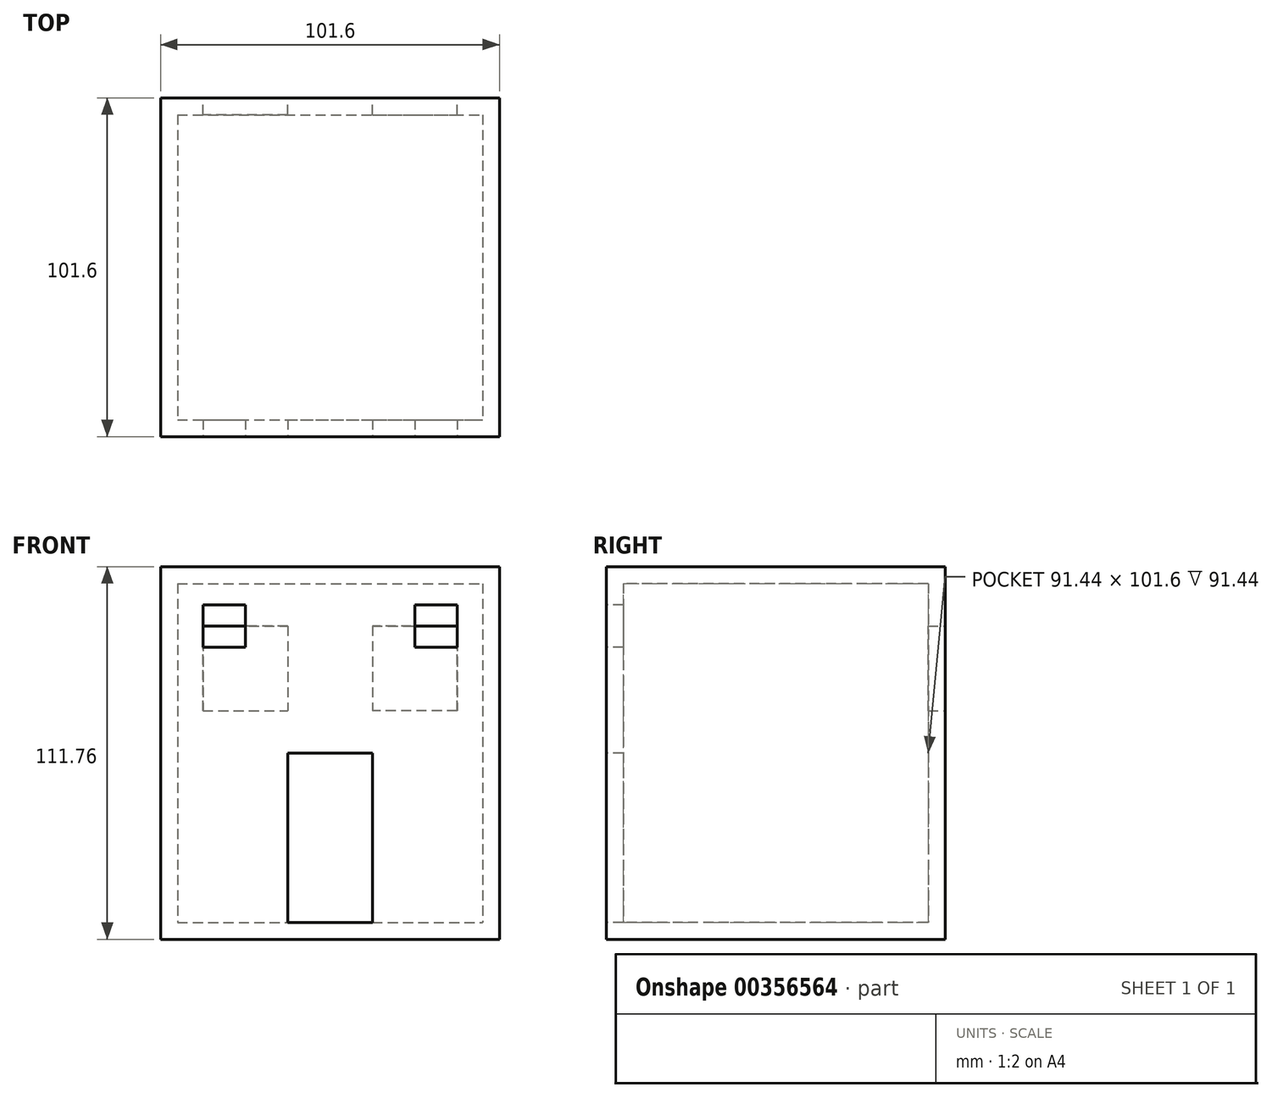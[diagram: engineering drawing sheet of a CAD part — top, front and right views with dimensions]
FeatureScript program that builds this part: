
annotation { "Feature Type Name" : "Feature", "Feature Type Description" : "" }
export const myFeature = defineFeature(function(context is Context, id is Id, definition is map)
    precondition{}
    {
        {
            var Q0;
            Q0=qCreatedBy(makeId("Top.planeOp"),FACE);
            var sketch = newSketch(context, id + "F0", { "sketchPlane" : qUnion([Q0])});
            skLineSegment(sketch, "E0.bottom", {"start": v(-50.8, 50.8) * mm, "end": v(50.8, 50.8) * mm});
            skLineSegment(sketch, "E0.top", {"start": v(-50.8, -50.8) * mm, "end": v(50.8, -50.8) * mm});
            skLineSegment(sketch, "E0.left", {"start": v(-50.8, 50.8) * mm, "end": v(-50.8, -50.8) * mm});
            skLineSegment(sketch, "E0.right", {"start": v(50.8, 50.8) * mm, "end": v(50.8, -50.8) * mm});
            skPoint(sketch, "E0.middle", {"position": v(0, 0) * mm});
            skSolve(sketch);
        }
        {
            var Q0;
            Q0 = qSketchRegion(id + "F0", true);
            extrude(context, id + "F1", {"entities" : qUnion([Q0]), "depth" : 5.08 * mm});
        }
        {
            var Q0;
            Q0=makeQuery(id+"F1.opExtrude","CAP_FACE",FACE,{"disambiguationData":[OSD([sQuery(id+"F0.wireOp",EDGE,"E0.bottom"),sQuery(id+"F0.wireOp",EDGE,"E0.top"),sQuery(id+"F0.wireOp",EDGE,"E0.left"),sQuery(id+"F0.wireOp",EDGE,"E0.right")])],"isStart":false});
            var sketch = newSketch(context, id + "F2", { "sketchPlane" : qUnion([Q0])});
            skLineSegment(sketch, "E1.bottom", {"start": v(-50.8, 50.8) * mm, "end": v(-45.72, 50.8) * mm});
            skLineSegment(sketch, "E1.top", {"start": v(-50.8, -50.8) * mm, "end": v(-45.72, -50.8) * mm});
            skLineSegment(sketch, "E1.left", {"start": v(-50.8, 50.8) * mm, "end": v(-50.8, -50.8) * mm});
            skLineSegment(sketch, "E1.right", {"start": v(-45.72, 50.8) * mm, "end": v(-45.72, -50.8) * mm});
            skLineSegment(sketch, "E2.bottom", {"start": v(50.8, 50.8) * mm, "end": v(45.72, 50.8) * mm});
            skLineSegment(sketch, "E2.top", {"start": v(50.8, -50.8) * mm, "end": v(45.72, -50.8) * mm});
            skLineSegment(sketch, "E2.left", {"start": v(50.8, 50.8) * mm, "end": v(50.8, -50.8) * mm});
            skLineSegment(sketch, "E2.right", {"start": v(45.72, 50.8) * mm, "end": v(45.72, -50.8) * mm});
            skLineSegment(sketch, "E3.bottom", {"start": v(-45.72, 50.8) * mm, "end": v(45.72, 50.8) * mm});
            skLineSegment(sketch, "E3.top", {"start": v(-45.72, 45.72) * mm, "end": v(45.72, 45.72) * mm});
            skLineSegment(sketch, "E3.left", {"start": v(-45.72, 50.8) * mm, "end": v(-45.72, 45.72) * mm});
            skLineSegment(sketch, "E3.right", {"start": v(45.72, 50.8) * mm, "end": v(45.72, 45.72) * mm});
            skLineSegment(sketch, "E4.bottom", {"start": v(-45.72, -50.8) * mm, "end": v(45.72, -50.8) * mm});
            skLineSegment(sketch, "E4.top", {"start": v(-45.72, -45.72) * mm, "end": v(45.72, -45.72) * mm});
            skLineSegment(sketch, "E4.left", {"start": v(-45.72, -50.8) * mm, "end": v(-45.72, -45.72) * mm});
            skLineSegment(sketch, "E4.right", {"start": v(45.72, -50.8) * mm, "end": v(45.72, -45.72) * mm});
            skSolve(sketch);
        }
        {
            var Q0;
            Q0 = qSketchRegion(id + "F2", true);
            extrude(context, id + "F3", {"entities" : qUnion([Q0]), "operationType" : NewBodyOperationType.ADD, "depth" : 101.6 * mm});
        }
        {
            var Q0;
            Q0=makeQuery(id+"F3.boolean.opBoolean","MERGE",FACE,{"derivedFrom":[makeQuery(id+"F1.opExtrude","SWEPT_FACE",FACE,{"disambiguationData":[OSD([sQuery(id+"F0.wireOp",EDGE,"E0.top")])]}),makeQuery(id+"F3.opExtrude","SWEPT_FACE",FACE,{"disambiguationData":[OSD([sQuery(id+"F2.wireOp",EDGE,"E1.top"),sQuery(id+"F2.wireOp",EDGE,"E2.top"),sQuery(id+"F2.wireOp",EDGE,"E4.bottom")])]})]});
            var sketch = newSketch(context, id + "F4", { "sketchPlane" : qUnion([Q0])});
            skLineSegment(sketch, "E5.bottom", {"start": v(-12.7, 55.88) * mm, "end": v(12.7, 55.88) * mm});
            skLineSegment(sketch, "E5.top", {"start": v(-12.7, 5.08) * mm, "end": v(12.7, 5.08) * mm});
            skLineSegment(sketch, "E5.left", {"start": v(-12.7, 55.88) * mm, "end": v(-12.7, 5.08) * mm});
            skLineSegment(sketch, "E5.right", {"start": v(12.7, 55.88) * mm, "end": v(12.7, 5.08) * mm});
            skLineSegment(sketch, "E6.bottom", {"start": v(-38.1, 100.33) * mm, "end": v(-25.4, 100.33) * mm});
            skLineSegment(sketch, "E6.top", {"start": v(-38.1, 87.63) * mm, "end": v(-25.4, 87.63) * mm});
            skLineSegment(sketch, "E6.left", {"start": v(-38.1, 100.33) * mm, "end": v(-38.1, 87.63) * mm});
            skLineSegment(sketch, "E6.right", {"start": v(-25.4, 100.33) * mm, "end": v(-25.4, 87.63) * mm});
            skPoint(sketch, "E7.firstSnap0", {"position": v(-31.75, 100.33) * mm});
            skLineSegment(sketch, "E7.bottom", {"start": v(25.4, 100.33) * mm, "end": v(38.1, 100.33) * mm});
            skLineSegment(sketch, "E7.top", {"start": v(25.4, 87.63) * mm, "end": v(38.1, 87.63) * mm});
            skLineSegment(sketch, "E7.left", {"start": v(25.4, 100.33) * mm, "end": v(25.4, 87.63) * mm});
            skLineSegment(sketch, "E7.right", {"start": v(38.1, 100.33) * mm, "end": v(38.1, 87.63) * mm});
            skSolve(sketch);
        }
        {
            var Q0;
            Q0=makeQuery(id+"F4.imprint","IMPRINT",FACE,{"disambiguationData":[TD([[makeQuery(id+"F4.imprint","IMPRINT",EDGE,{"derivedFrom":sQuery(id+"F4.wireOp",EDGE,"E5.bottom")}),-1.0]])]});
            var Q1;
            Q1=makeQuery(id+"F4.imprint","IMPRINT",FACE,{"disambiguationData":[TD([[makeQuery(id+"F4.imprint","IMPRINT",EDGE,{"derivedFrom":sQuery(id+"F4.wireOp",EDGE,"E6.bottom")}),-1.0]])]});
            var Q2;
            Q2=makeQuery(id+"F4.imprint","IMPRINT",FACE,{"disambiguationData":[TD([[makeQuery(id+"F4.imprint","IMPRINT",EDGE,{"derivedFrom":sQuery(id+"F4.wireOp",EDGE,"E7.bottom")}),-1.0]])]});
            extrude(context, id + "F5", {"entities" : qUnion([Q0, Q1, Q2]), "operationType" : NewBodyOperationType.REMOVE, "endBound" : BoundingType.UP_TO_NEXT, "oppositeDirection" : true, "depth" : 25.4 * mm});
        }
        {
            var Q0;
            Q0=makeQuery(id+"F3.boolean.opBoolean","MERGE",FACE,{"derivedFrom":[makeQuery(id+"F1.opExtrude","SWEPT_FACE",FACE,{"disambiguationData":[OSD([sQuery(id+"F0.wireOp",EDGE,"E0.bottom")])]}),makeQuery(id+"F3.opExtrude","SWEPT_FACE",FACE,{"disambiguationData":[OSD([sQuery(id+"F2.wireOp",EDGE,"E1.bottom"),sQuery(id+"F2.wireOp",EDGE,"E2.bottom"),sQuery(id+"F2.wireOp",EDGE,"E3.bottom")])]})]});
            var sketch = newSketch(context, id + "F6", { "sketchPlane" : qUnion([Q0])});
            skLineSegment(sketch, "E8.bottom", {"start": v(-38.1, 93.98) * mm, "end": v(-12.7, 93.98) * mm});
            skLineSegment(sketch, "E8.top", {"start": v(-38.1, 68.58) * mm, "end": v(-12.7, 68.58) * mm});
            skLineSegment(sketch, "E8.left", {"start": v(-38.1, 93.98) * mm, "end": v(-38.1, 68.58) * mm});
            skLineSegment(sketch, "E8.right", {"start": v(-12.7, 93.98) * mm, "end": v(-12.7, 68.58) * mm});
            skLineSegment(sketch, "E9.MirrorCS", {"start": v(12.7, 93.98) * mm, "end": v(12.7, 68.58) * mm});
            skLineSegment(sketch, "E10.MirrorCS", {"start": v(38.1, 93.98) * mm, "end": v(12.7, 93.98) * mm});
            skLineSegment(sketch, "E11.MirrorCS", {"start": v(38.1, 93.98) * mm, "end": v(38.1, 68.58) * mm});
            skLineSegment(sketch, "E12.MirrorCS", {"start": v(38.1, 68.58) * mm, "end": v(12.7, 68.58) * mm});
            skSolve(sketch);
        }
        {
            var Q0;
            Q0=makeQuery(id+"F6.imprint","IMPRINT",FACE,{"disambiguationData":[TD([[makeQuery(id+"F6.imprint","IMPRINT",EDGE,{"derivedFrom":sQuery(id+"F6.wireOp",EDGE,"E8.bottom")}),-1.0]])]});
            var Q1;
            Q1=makeQuery(id+"F6.imprint","IMPRINT",FACE,{"disambiguationData":[TD([[makeQuery(id+"F6.imprint","IMPRINT",EDGE,{"derivedFrom":sQuery(id+"F6.wireOp",EDGE,"E9.MirrorCS")}),1.0]])]});
            extrude(context, id + "F7", {"entities" : qUnion([Q0, Q1]), "operationType" : NewBodyOperationType.REMOVE, "endBound" : BoundingType.UP_TO_NEXT, "oppositeDirection" : true, "depth" : 25.4 * mm});
        }
        {
            var Q0;
            Q0=makeQuery(id+"F3.opExtrude","CAP_FACE",FACE,{"disambiguationData":[OSD([sQuery(id+"F2.wireOp",EDGE,"E1.bottom"),sQuery(id+"F2.wireOp",EDGE,"E1.top"),sQuery(id+"F2.wireOp",EDGE,"E1.left"),sQuery(id+"F2.wireOp",EDGE,"E1.right"),sQuery(id+"F2.wireOp",EDGE,"E2.bottom"),sQuery(id+"F2.wireOp",EDGE,"E2.top"),sQuery(id+"F2.wireOp",EDGE,"E2.left"),sQuery(id+"F2.wireOp",EDGE,"E2.right"),sQuery(id+"F2.wireOp",EDGE,"E3.bottom"),sQuery(id+"F2.wireOp",EDGE,"E3.top"),sQuery(id+"F2.wireOp",EDGE,"E4.bottom"),sQuery(id+"F2.wireOp",EDGE,"E4.top")])],"isStart":false});
            var sketch = newSketch(context, id + "F8", { "sketchPlane" : qUnion([Q0])});
            skLineSegment(sketch, "E13.bottom", {"start": v(-50.8, 50.8) * mm, "end": v(50.8, 50.8) * mm});
            skLineSegment(sketch, "E13.top", {"start": v(-50.8, -50.8) * mm, "end": v(50.8, -50.8) * mm});
            skLineSegment(sketch, "E13.left", {"start": v(-50.8, 50.8) * mm, "end": v(-50.8, -50.8) * mm});
            skLineSegment(sketch, "E13.right", {"start": v(50.8, 50.8) * mm, "end": v(50.8, -50.8) * mm});
            skSolve(sketch);
        }
        {
            var Q0;
            Q0 = qSketchRegion(id + "F8", true);
            extrude(context, id + "F9", {"entities" : qUnion([Q0]), "operationType" : NewBodyOperationType.ADD, "depth" : 5.08 * mm});
        }
    });
